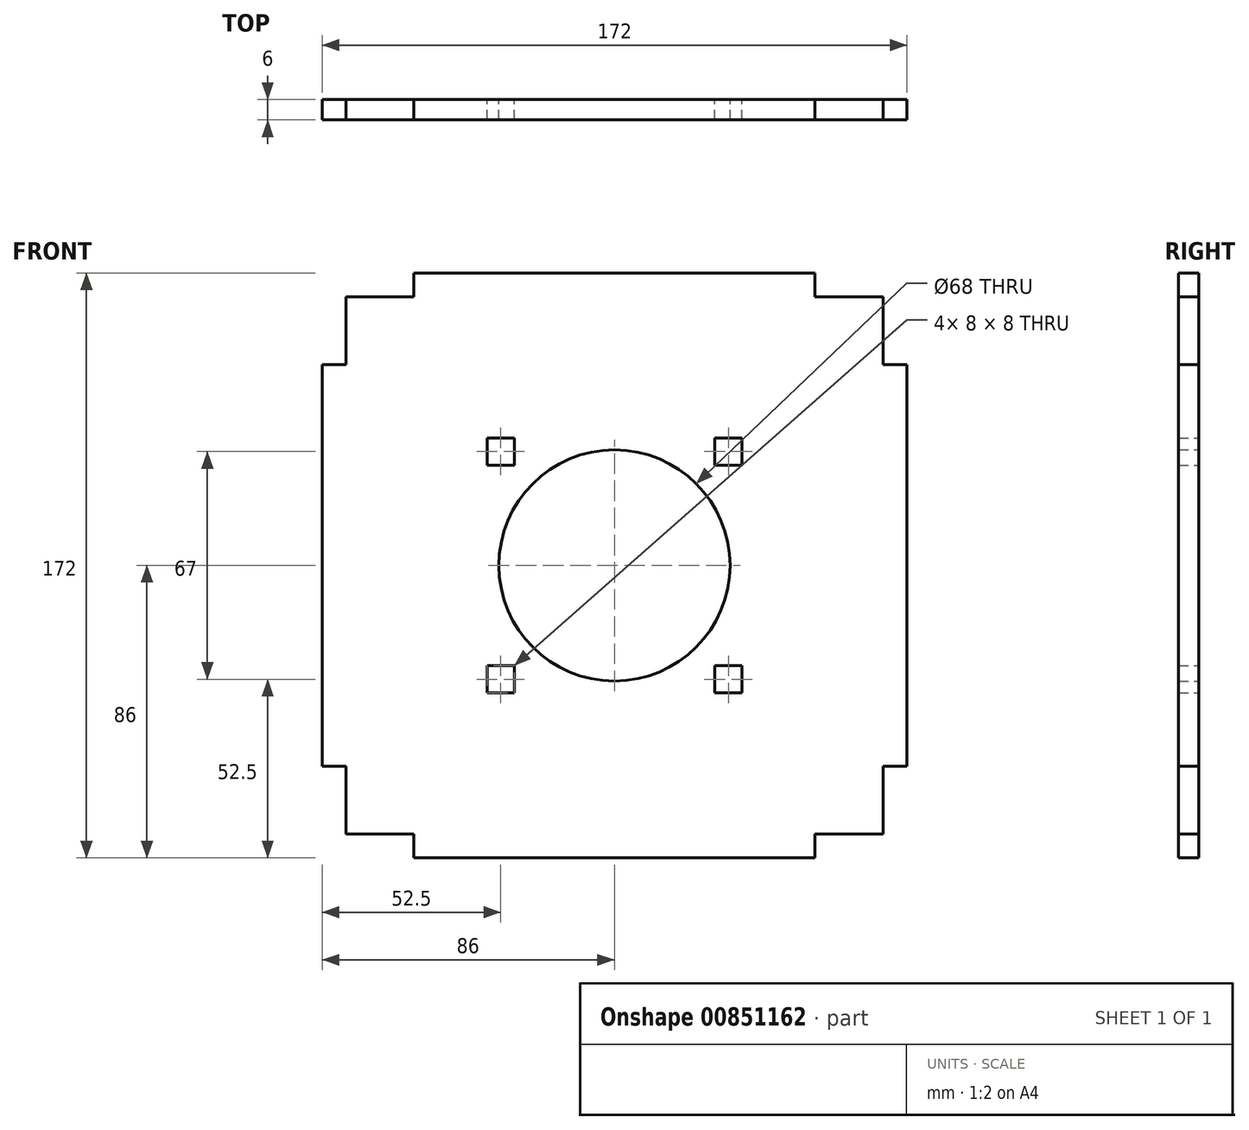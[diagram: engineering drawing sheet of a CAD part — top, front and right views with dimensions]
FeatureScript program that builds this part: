
annotation { "Feature Type Name" : "Feature", "Feature Type Description" : "" }
export const myFeature = defineFeature(function(context is Context, id is Id, definition is map)
    precondition{}
    {
        {
            var Q0;
            Q0=qCreatedBy(makeId("Front.planeOp"),FACE);
            var sketch = newSketch(context, id + "F0", { "sketchPlane" : qUnion([Q0])});
            skLineSegment(sketch, "E0.bottom", {"start": v(59, 86) * mm, "end": v(-59, 86) * mm});
            skLineSegment(sketch, "E0.top", {"start": v(59, -86) * mm, "end": v(-59, -86) * mm});
            skLineSegment(sketch, "E0.left", {"start": v(86, 59) * mm, "end": v(86, -59) * mm});
            skLineSegment(sketch, "E0.right", {"start": v(-86, 59) * mm, "end": v(-86, -59) * mm});
            skPoint(sketch, "E0.middle", {"position": v(0, 0) * mm});
            skLineSegment(sketch, "E1", {"start": v(-86, -59) * mm, "end": v(-79, -59) * mm});
            skLineSegment(sketch, "E2", {"start": v(-79, -59) * mm, "end": v(-79, -79) * mm});
            skLineSegment(sketch, "E3", {"start": v(-79, -79) * mm, "end": v(-59, -79) * mm});
            skLineSegment(sketch, "E4", {"start": v(-59, -79) * mm, "end": v(-59, -86) * mm});
            skLineSegment(sketch, "E5.MirrorCS", {"start": v(86, -59) * mm, "end": v(79, -59) * mm});
            skLineSegment(sketch, "E6.MirrorCS", {"start": v(79, -59) * mm, "end": v(79, -79) * mm});
            skLineSegment(sketch, "E7.MirrorCS", {"start": v(79, -79) * mm, "end": v(59, -79) * mm});
            skLineSegment(sketch, "E8.MirrorCS", {"start": v(59, -79) * mm, "end": v(59, -86) * mm});
            skPoint(sketch, "E9.orphan", {"position": v(-86, -86) * mm});
            skPoint(sketch, "E10.orphan", {"position": v(86, -86) * mm});
            skPoint(sketch, "E11.orphan", {"position": v(-86, 86) * mm});
            skPoint(sketch, "E12.orphan", {"position": v(86, 86) * mm});
            skLineSegment(sketch, "E13.MirrorCS", {"start": v(86, 59) * mm, "end": v(79, 59) * mm});
            skLineSegment(sketch, "E14.MirrorCS", {"start": v(-59, 79) * mm, "end": v(-59, 86) * mm});
            skLineSegment(sketch, "E15.MirrorCS", {"start": v(59, 79) * mm, "end": v(59, 86) * mm});
            skLineSegment(sketch, "E16.MirrorCS", {"start": v(-86, 59) * mm, "end": v(-79, 59) * mm});
            skLineSegment(sketch, "E17.MirrorCS", {"start": v(79, 79) * mm, "end": v(59, 79) * mm});
            skLineSegment(sketch, "E18.MirrorCS", {"start": v(-79, 79) * mm, "end": v(-59, 79) * mm});
            skLineSegment(sketch, "E19.MirrorCS", {"start": v(79, 59) * mm, "end": v(79, 79) * mm});
            skLineSegment(sketch, "E20.MirrorCS", {"start": v(-79, 59) * mm, "end": v(-79, 79) * mm});
            skPoint(sketch, "E21.right.end.orphan", {"position": v(-79, 79) * mm});
            skPoint(sketch, "E21.right.start.orphan", {"position": v(-79, 86) * mm});
            skPoint(sketch, "E22.orphan", {"position": v(-86, 79) * mm});
            skPoint(sketch, "E23.MirrorCS.end.orphan", {"position": v(79, 79) * mm});
            skPoint(sketch, "E23.MirrorCS.start.orphan", {"position": v(79, 86) * mm});
            skPoint(sketch, "E24.orphan", {"position": v(86, 79) * mm});
            skCircle(sketch, "E25", {"center": v(0, 0) * mm, "radius": 34 * mm});
            skPoint(sketch, "E26.orphan", {"position": v(-33.5, 33.5) * mm});
            skPoint(sketch, "E27.orphan", {"position": v(33.5, 33.5) * mm});
            skPoint(sketch, "E28.orphan", {"position": v(-33.5, -33.5) * mm});
            skPoint(sketch, "E29.top.start.orphan", {"position": v(33.5, -33.5) * mm});
            skLineSegment(sketch, "E30.bottom", {"start": v(29.5, 37.5) * mm, "end": v(37.5, 37.5) * mm});
            skLineSegment(sketch, "E30.top", {"start": v(29.5, 29.5) * mm, "end": v(37.5, 29.5) * mm});
            skLineSegment(sketch, "E30.left", {"start": v(29.5, 37.5) * mm, "end": v(29.5, 29.5) * mm});
            skLineSegment(sketch, "E30.right", {"start": v(37.5, 37.5) * mm, "end": v(37.5, 29.5) * mm});
            skLineSegment(sketch, "E31.MirrorCS", {"start": v(-29.5, 29.5) * mm, "end": v(-37.5, 29.5) * mm});
            skLineSegment(sketch, "E32.MirrorCS", {"start": v(-37.5, 37.5) * mm, "end": v(-37.5, 29.5) * mm});
            skLineSegment(sketch, "E33.MirrorCS", {"start": v(-29.5, 37.5) * mm, "end": v(-29.5, 29.5) * mm});
            skLineSegment(sketch, "E34.MirrorCS", {"start": v(-29.5, 37.5) * mm, "end": v(-37.5, 37.5) * mm});
            skLineSegment(sketch, "E35.MirrorCS", {"start": v(37.5, -37.5) * mm, "end": v(37.5, -29.5) * mm});
            skLineSegment(sketch, "E36.MirrorCS", {"start": v(29.5, -29.5) * mm, "end": v(37.5, -29.5) * mm});
            skLineSegment(sketch, "E37.MirrorCS", {"start": v(29.5, -37.5) * mm, "end": v(37.5, -37.5) * mm});
            skLineSegment(sketch, "E38.MirrorCS", {"start": v(29.5, -37.5) * mm, "end": v(29.5, -29.5) * mm});
            skLineSegment(sketch, "E39.MirrorCS", {"start": v(-29.5, -37.5) * mm, "end": v(-29.5, -29.5) * mm});
            skLineSegment(sketch, "E40.MirrorCS", {"start": v(-29.5, -29.5) * mm, "end": v(-37.5, -29.5) * mm});
            skLineSegment(sketch, "E41.MirrorCS", {"start": v(-29.5, -37.5) * mm, "end": v(-37.5, -37.5) * mm});
            skLineSegment(sketch, "E42.MirrorCS", {"start": v(-37.5, -37.5) * mm, "end": v(-37.5, -29.5) * mm});
            skSolve(sketch);
        }
        {
            var Q0;
            Q0=qSketchRegion(id+"F0",true);
            extrude(context, id + "F1", {"entities" : qUnion([Q0]), "depth" : 6 * mm, "offsetDistance" : 25 * mm});
        }
    });
